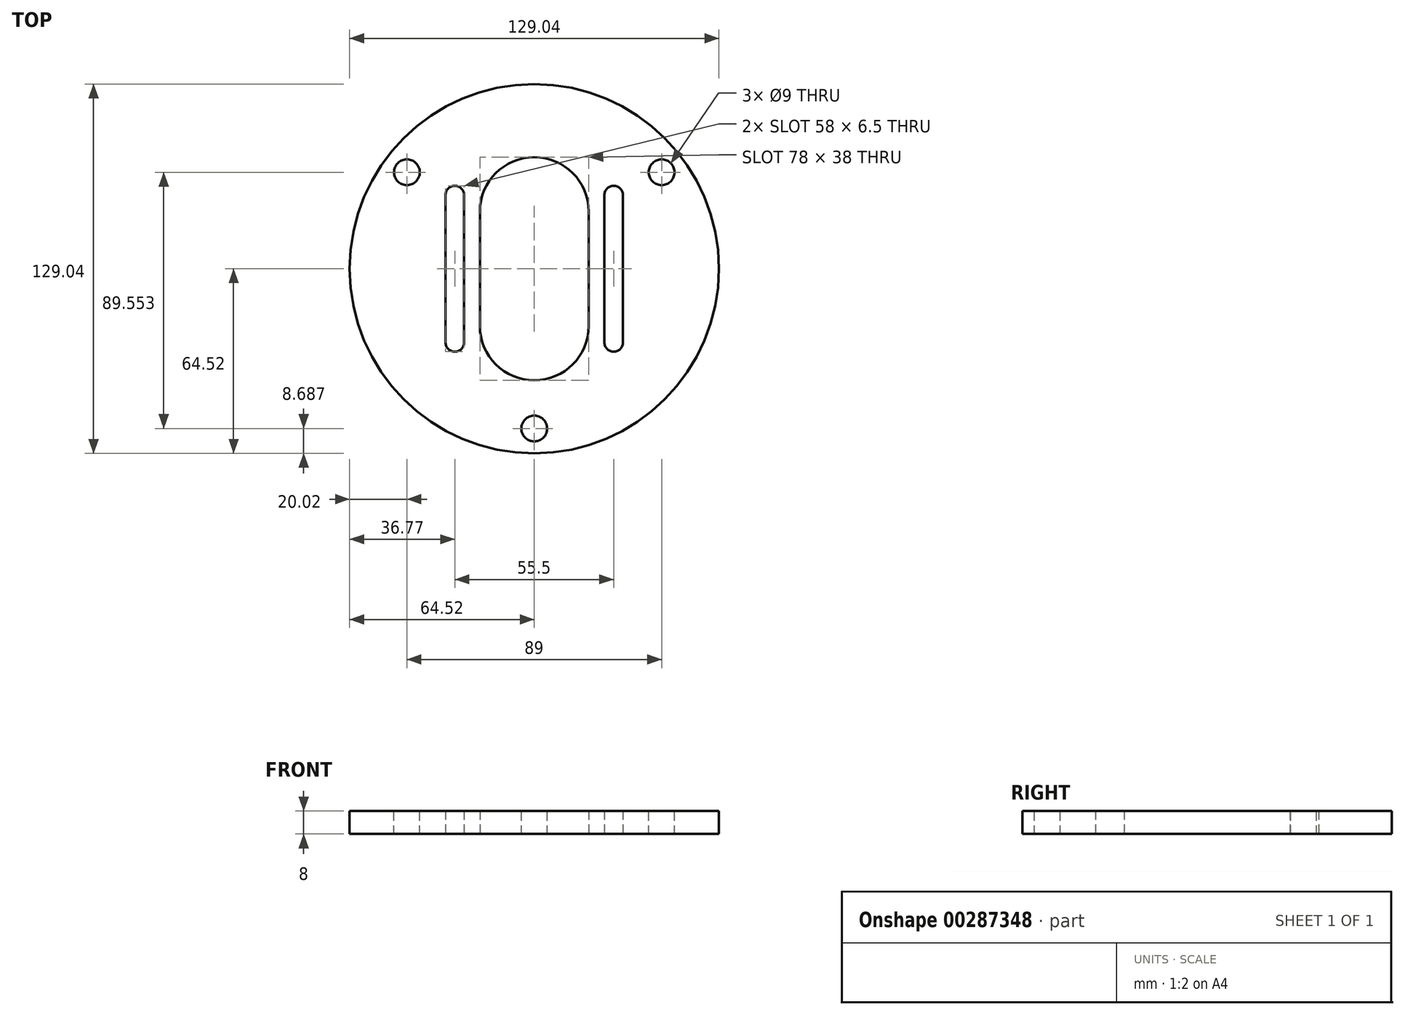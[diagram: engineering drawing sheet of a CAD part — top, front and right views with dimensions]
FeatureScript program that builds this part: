
annotation { "Feature Type Name" : "Feature", "Feature Type Description" : "" }
export const myFeature = defineFeature(function(context is Context, id is Id, definition is map)
    precondition{}
    {
        {
            var Q0;
            Q0=qCreatedBy(makeId("Top.planeOp"),FACE);
            var sketch = newSketch(context, id + "F0", { "sketchPlane" : qUnion([Q0])});
            skCircle(sketch, "E0", {"center": v(0, 0) * mm, "radius": 64.52 * mm});
            skSolve(sketch);
        }
        {
            var Q0;
            Q0=qCreatedBy(makeId("Top.planeOp"),FACE);
            var sketch = newSketch(context, id + "F1", { "sketchPlane" : qUnion([Q0])});
            skLineSegment(sketch, "E1", {"start": v(-19, 0) * mm, "end": v(-19, 20) * mm});
            skArc(sketch, "E2", {"start": v(-19, 20) * mm, "mid": v(-13.44, 33.44) * mm, "end": v(0, 39) * mm});
            skLineSegment(sketch, "E3", {"start": v(-24.5, 0) * mm, "end": v(-24.5, 25.75) * mm});
            skLineSegment(sketch, "E4", {"start": v(-31, 0) * mm, "end": v(-31, 25.75) * mm});
            skArc(sketch, "E5", {"start": v(-31, 25.75) * mm, "mid": v(-27.75, 29) * mm, "end": v(-24.5, 25.75) * mm});
            skPoint(sketch, "E6", {"position": v(-27.75, 29) * mm});
            skArc(sketch, "E7.MirrorCS", {"start": v(19, 20) * mm, "mid": v(13.44, 33.44) * mm, "end": v(0, 39) * mm});
            skLineSegment(sketch, "E8.MirrorCS", {"start": v(19, 0) * mm, "end": v(19, 20) * mm});
            skLineSegment(sketch, "E9.MirrorCS", {"start": v(24.5, 0) * mm, "end": v(24.5, 25.75) * mm});
            skPoint(sketch, "E10.MirrorP", {"position": v(27.75, 29) * mm});
            skArc(sketch, "E11.MirrorCS", {"start": v(31, 25.75) * mm, "mid": v(27.75, 29) * mm, "end": v(24.5, 25.75) * mm});
            skLineSegment(sketch, "E12.MirrorCS", {"start": v(31, 0) * mm, "end": v(31, 25.75) * mm});
            skPoint(sketch, "E13.MirrorP", {"position": v(27.75, -29) * mm});
            skLineSegment(sketch, "E14.MirrorCS", {"start": v(31, 0) * mm, "end": v(31, -25.75) * mm});
            skArc(sketch, "E15.MirrorCS", {"start": v(31, -25.75) * mm, "mid": v(27.75, -29) * mm, "end": v(24.5, -25.75) * mm});
            skLineSegment(sketch, "E16.MirrorCS", {"start": v(24.5, 0) * mm, "end": v(24.5, -25.75) * mm});
            skArc(sketch, "E17.MirrorCS", {"start": v(-31, -25.75) * mm, "mid": v(-27.75, -29) * mm, "end": v(-24.5, -25.75) * mm});
            skPoint(sketch, "E18.MirrorP", {"position": v(-27.75, -29) * mm});
            skLineSegment(sketch, "E19.MirrorCS", {"start": v(-31, 0) * mm, "end": v(-31, -25.75) * mm});
            skLineSegment(sketch, "E20.MirrorCS", {"start": v(-24.5, 0) * mm, "end": v(-24.5, -25.75) * mm});
            skLineSegment(sketch, "E21.MirrorCS", {"start": v(19, 0) * mm, "end": v(19, -20) * mm});
            skArc(sketch, "E22.MirrorCS", {"start": v(19, -20) * mm, "mid": v(13.44, -33.44) * mm, "end": v(0, -39) * mm});
            skLineSegment(sketch, "E23.MirrorCS", {"start": v(-19, 0) * mm, "end": v(-19, -20) * mm});
            skArc(sketch, "E24.MirrorCS", {"start": v(-19, -20) * mm, "mid": v(-13.44, -33.44) * mm, "end": v(0, -39) * mm});
            skSolve(sketch);
        }
        {
            var Q0;
            Q0 = qSketchRegion(id + "F0", true);
            extrude(context, id + "F2", {"entities" : qUnion([Q0]), "depth" : 8 * mm});
        }
        {
            var Q0;
            Q0 = qSketchRegion(id + "F1", true);
            extrude(context, id + "F3", {"entities" : qUnion([Q0]), "operationType" : NewBodyOperationType.REMOVE, "endBound" : BoundingType.UP_TO_NEXT, "depth" : 25 * mm});
        }
        {
            var Q0;
            Q0=makeQuery(id+"F2.opExtrude","CAP_FACE",FACE,{"disambiguationData":[OSD([sQuery(id+"F0.wireOp",EDGE,"E0")])],"isStart":false});
            var sketch = newSketch(context, id + "F4", { "sketchPlane" : qUnion([Q0])});
            skCircle(sketch, "E25", {"center": v(0, -55.83) * mm, "radius": 4.5 * mm});
            skCircle(sketch, "E26", {"center": v(-44.5, 33.72) * mm, "radius": 4.5 * mm});
            skLineSegment(sketch, "E27", {"start": v(-44.5, 33.72) * mm, "end": v(0, -55.83) * mm, "construction": true});
            skLineSegment(sketch, "E28", {"start": v(-44.5, 33.72) * mm, "end": v(0, 0) * mm, "construction": true});
            skLineSegment(sketch, "E29", {"start": v(0, 0) * mm, "end": v(0, -55.83) * mm, "construction": true});
            skCircle(sketch, "E30.MirrorC", {"center": v(44.5, 33.72) * mm, "radius": 4.5 * mm});
            skSolve(sketch);
        }
        {
            var Q0;
            Q0 = qSketchRegion(id + "F4", true);
            extrude(context, id + "F5", {"entities" : qUnion([Q0]), "operationType" : NewBodyOperationType.REMOVE, "endBound" : BoundingType.UP_TO_NEXT, "oppositeDirection" : true, "depth" : 25 * mm});
        }
    });
